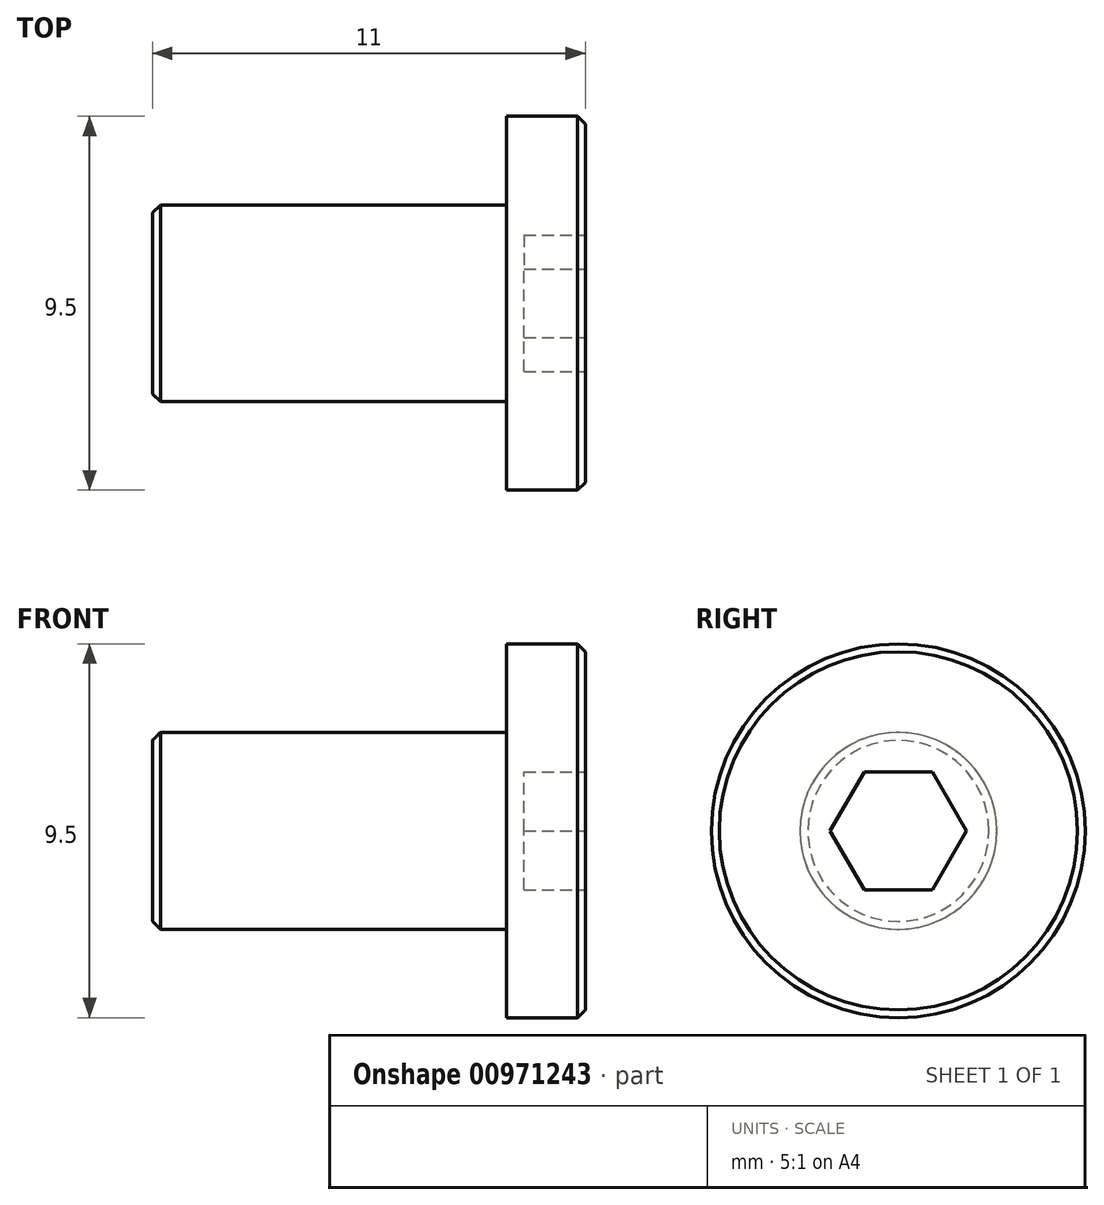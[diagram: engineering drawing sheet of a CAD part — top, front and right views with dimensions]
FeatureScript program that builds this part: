
annotation { "Feature Type Name" : "Feature", "Feature Type Description" : "" }
export const myFeature = defineFeature(function(context is Context, id is Id, definition is map)
    precondition{}
    {
        {
            var Q0;
            Q0=qCreatedBy(makeId("Front.planeOp"),FACE);
            var sketch = newSketch(context, id + "F0", { "sketchPlane" : qUnion([Q0])});
            skLineSegment(sketch, "E0.bottom", {"start": v(4.04, 36) * mm, "end": v(-4.96, 36) * mm});
            skLineSegment(sketch, "E0.top", {"start": v(4.04, 33.5) * mm, "end": v(-4.96, 33.5) * mm});
            skLineSegment(sketch, "E0.left", {"start": v(4.04, 36) * mm, "end": v(4.04, 33.5) * mm});
            skLineSegment(sketch, "E0.right", {"start": v(-4.96, 36) * mm, "end": v(-4.96, 33.5) * mm});
            skLineSegment(sketch, "E1.bottom", {"start": v(4.04, 33.5) * mm, "end": v(6.04, 33.5) * mm});
            skLineSegment(sketch, "E1.top", {"start": v(4.04, 38.26) * mm, "end": v(6.04, 38.26) * mm});
            skLineSegment(sketch, "E1.left", {"start": v(4.04, 33.5) * mm, "end": v(4.04, 38.26) * mm});
            skLineSegment(sketch, "E1.right", {"start": v(6.04, 33.5) * mm, "end": v(6.04, 38.26) * mm});
            skSolve(sketch);
        }
        {
            var Q0;
            Q0=qSketchRegion(id+"F0",true);
            var Q1;
            Q1=sQuery(id+"F0.wireOp",EDGE,"E0.top");
            revolve(context, id + "F1", {"surfaceOperationType" : NewSurfaceOperationType.NEW, "entities" : qUnion([Q0]), "axis" : qUnion([Q1]), "revolveType" : RevolveType.FULL});
        }
        {
            var Q0;
            Q0=makeQuery(id+"F1.opRevolve","SWEPT_EDGE",EDGE,{"disambiguationData":[OSD([sQuery(id+"F0.wireOp",EDGE,"E0.bottom"),sQuery(id+"F0.wireOp",EDGE,"E0.right")])]});
            var Q1;
            Q1=makeQuery(id+"F1.opRevolve","SWEPT_EDGE",EDGE,{"disambiguationData":[OSD([sQuery(id+"F0.wireOp",EDGE,"E1.top"),sQuery(id+"F0.wireOp",EDGE,"E1.right")])]});
            chamfer(context, id + "F2", {"entities" : qUnion([Q0, Q1]), "width" : 0.2 * mm, "tangentPropagation" : true});
        }
        {
            var Q0;
            Q0=makeQuery(id+"F1.opRevolve","SWEPT_FACE",FACE,{"disambiguationData":[OSD([sQuery(id+"F0.wireOp",EDGE,"E1.right")])]});
            var sketch = newSketch(context, id + "F3", { "sketchPlane" : qUnion([Q0])});
            skCircle(sketch, "E2.cCircle", {"center": v(0, 33.5) * mm, "radius": 1.5 * mm, "construction": true});
            skLineSegment(sketch, "E2.0", {"start": v(-0.87, 35) * mm, "end": v(0.87, 35) * mm});
            skLineSegment(sketch, "E2.1", {"start": v(0.87, 35) * mm, "end": v(1.73, 33.5) * mm});
            skLineSegment(sketch, "E2.2", {"start": v(1.73, 33.5) * mm, "end": v(0.87, 32) * mm});
            skLineSegment(sketch, "E2.3", {"start": v(0.87, 32) * mm, "end": v(-0.87, 32) * mm});
            skLineSegment(sketch, "E2.4", {"start": v(-0.87, 32) * mm, "end": v(-1.73, 33.5) * mm});
            skLineSegment(sketch, "E2.5", {"start": v(-1.73, 33.5) * mm, "end": v(-0.87, 35) * mm});
            skPoint(sketch, "E2.0.midPoint", {"position": v(0, 35) * mm});
            skSolve(sketch);
        }
        {
            var Q0;
            Q0=qSketchRegion(id+"F3",true);
            extrude(context, id + "F4", {"entities" : qUnion([Q0]), "operationType" : NewBodyOperationType.REMOVE, "oppositeDirection" : true, "depth" : 1.56 * mm, "offsetDistance" : 25 * mm});
        }
    });
